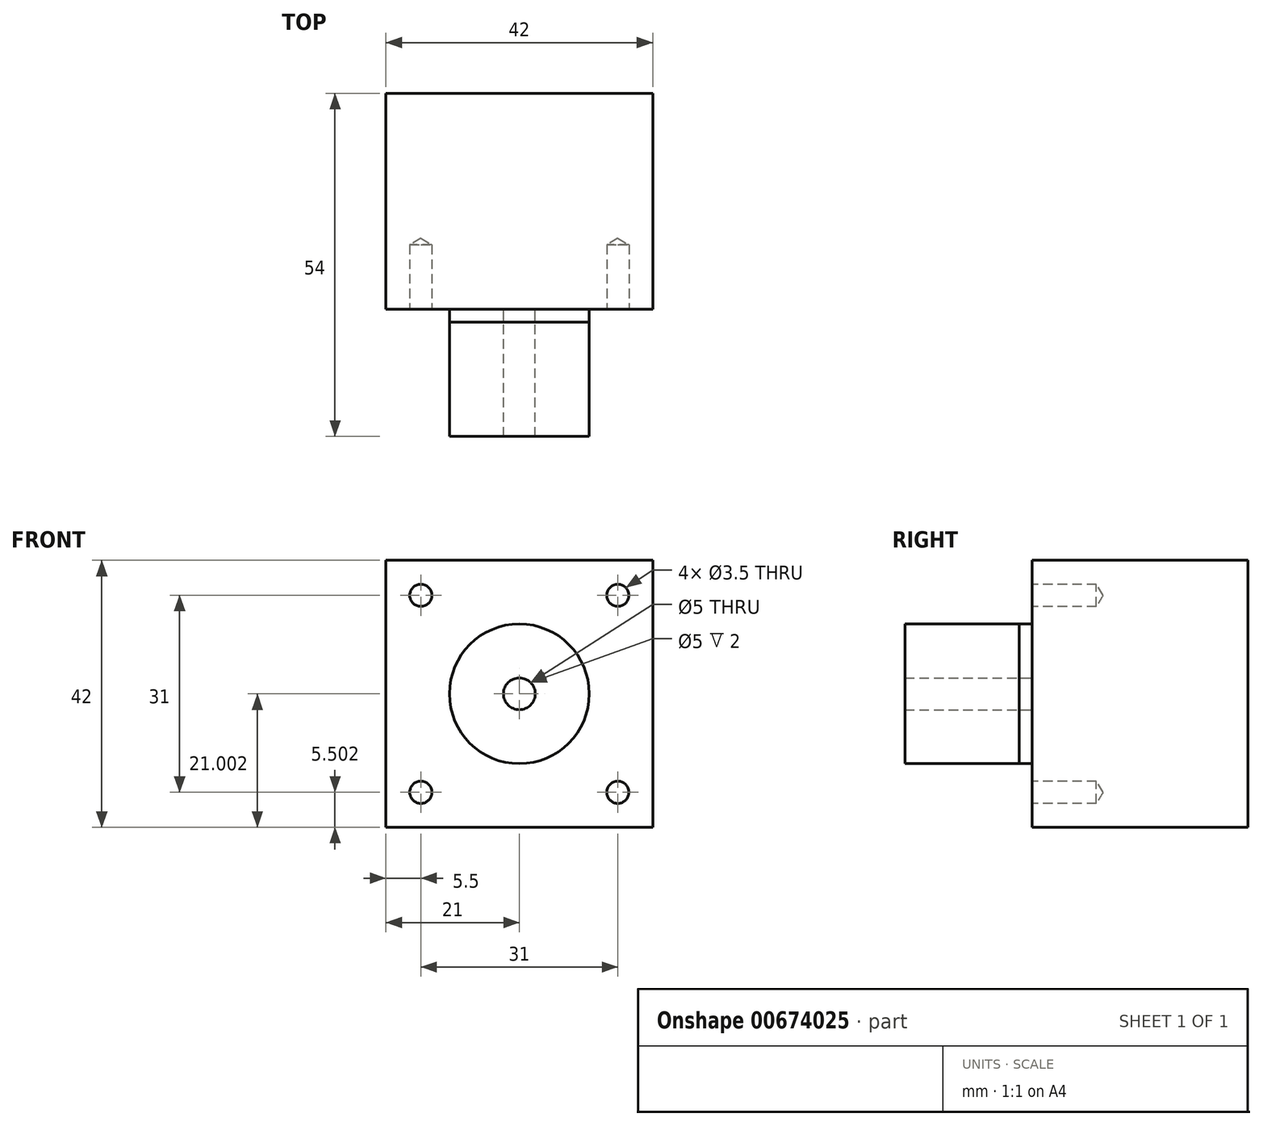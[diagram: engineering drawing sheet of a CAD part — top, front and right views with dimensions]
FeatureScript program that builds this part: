
annotation { "Feature Type Name" : "Feature", "Feature Type Description" : "" }
export const myFeature = defineFeature(function(context is Context, id is Id, definition is map)
    precondition{}
    {
        {
            var Q0;
            Q0=qCreatedBy(makeId("Right.planeOp"),FACE);
            var sketch = newSketch(context, id + "F0", { "sketchPlane" : qUnion([Q0])});
            skLineSegment(sketch, "E0.bottom", {"start": v(-63.29, 37.38) * mm, "end": v(-29.29, 37.38) * mm});
            skLineSegment(sketch, "E0.top", {"start": v(-63.29, 16.38) * mm, "end": v(-29.29, 16.38) * mm, "construction": true});
            skLineSegment(sketch, "E0.left", {"start": v(-63.29, 37.38) * mm, "end": v(-63.29, 16.38) * mm});
            skLineSegment(sketch, "E0.right", {"start": v(-29.29, 37.38) * mm, "end": v(-29.29, 16.38) * mm});
            skLineSegment(sketch, "E1.bottom", {"start": v(-63.29, 16.38) * mm, "end": v(-65.29, 16.38) * mm, "construction": true});
            skLineSegment(sketch, "E1.top", {"start": v(-63.29, 27.38) * mm, "end": v(-65.29, 27.38) * mm});
            skLineSegment(sketch, "E1.left", {"start": v(-63.29, 16.38) * mm, "end": v(-63.29, 27.38) * mm});
            skLineSegment(sketch, "E1.right", {"start": v(-65.29, 16.38) * mm, "end": v(-65.29, 27.38) * mm});
            skLineSegment(sketch, "E2.bottom", {"start": v(-65.29, 16.38) * mm, "end": v(-83.29, 16.38) * mm, "construction": true});
            skLineSegment(sketch, "E2.top", {"start": v(-65.29, 18.88) * mm, "end": v(-68.29, 18.88) * mm});
            skLineSegment(sketch, "E2.left", {"start": v(-65.29, 16.38) * mm, "end": v(-65.29, 18.88) * mm});
            skLineSegment(sketch, "E2.right", {"start": v(-83.29, 16.38) * mm, "end": v(-83.29, 18.38) * mm});
            skLineSegment(sketch, "E3.MirrorCS", {"start": v(-63.29, 5.38) * mm, "end": v(-65.29, 5.38) * mm});
            skLineSegment(sketch, "E4.MirrorCS", {"start": v(-63.29, 16.38) * mm, "end": v(-63.29, 5.38) * mm});
            skLineSegment(sketch, "E5.MirrorCS", {"start": v(-65.29, 16.38) * mm, "end": v(-65.29, 5.38) * mm});
            skLineSegment(sketch, "E6.MirrorCS", {"start": v(-29.29, -4.62) * mm, "end": v(-29.29, 16.38) * mm});
            skLineSegment(sketch, "E7.MirrorCS", {"start": v(-63.29, -4.62) * mm, "end": v(-29.29, -4.62) * mm});
            skLineSegment(sketch, "E8.MirrorCS", {"start": v(-65.29, 16.38) * mm, "end": v(-65.29, 13.88) * mm});
            skLineSegment(sketch, "E9.MirrorCS", {"start": v(-83.29, 16.38) * mm, "end": v(-83.29, 13.88) * mm});
            skLineSegment(sketch, "E10.MirrorCS", {"start": v(-65.29, 13.88) * mm, "end": v(-83.29, 13.88) * mm});
            skLineSegment(sketch, "E11.MirrorCS", {"start": v(-63.29, -4.62) * mm, "end": v(-63.29, 16.38) * mm});
            skLineSegment(sketch, "E12", {"start": v(-83.29, 18.38) * mm, "end": v(-68.29, 18.38) * mm});
            skLineSegment(sketch, "E13", {"start": v(-68.29, 18.38) * mm, "end": v(-68.29, 18.88) * mm});
            skSolve(sketch);
        }
        {
            var Q0;
            Q0=makeQuery(id+"F0.imprint","IMPRINT",FACE,{"disambiguationData":[TD([[makeQuery(id+"F0.imprint","IMPRINT",EDGE,{"derivedFrom":sQuery(id+"F0.wireOp",EDGE,"E0.bottom")}),-1.0]])]});
            extrude(context, id + "F1", {"entities" : qUnion([Q0]), "endBound" : BoundingType.SYMMETRIC, "depth" : 42 * mm, "offsetDistance" : 25.4 * mm});
        }
        {
            var Q0;
            Q0=makeQuery(id+"F1.opExtrude","SWEPT_FACE",FACE,{"disambiguationData":[OSD([sQuery(id+"F0.wireOp",EDGE,"E0.left"),sQuery(id+"F0.wireOp",EDGE,"E1.left"),sQuery(id+"F0.wireOp",EDGE,"E11.MirrorCS")])]});
            var sketch = newSketch(context, id + "F2", { "sketchPlane" : qUnion([Q0])});
            skLineSegment(sketch, "E14.0", {"start": v(0, 16.38) * mm, "end": v(0, 13.88) * mm});
            skLineSegment(sketch, "E15.0", {"start": v(0, 16.38) * mm, "end": v(0, 18.38) * mm});
            skLineSegment(sketch, "E16.0", {"start": v(0, 18.38) * mm, "end": v(0, 18.88) * mm});
            skLineSegment(sketch, "E17.0", {"start": v(0, 16.38) * mm, "end": v(0, 5.38) * mm});
            skLineSegment(sketch, "E18.0", {"start": v(0, 16.38) * mm, "end": v(0, 27.38) * mm});
            skCircle(sketch, "E19", {"center": v(0, 16.38) * mm, "radius": 11 * mm});
            skCircle(sketch, "E20", {"center": v(0, 16.38) * mm, "radius": 2.5 * mm});
            skSolve(sketch);
        }
        {
            var Q0;
            {var subQ0=sQuery(id+"F2.wireOp",EDGE,"E19");var subQ1=sQuery(id+"F2.wireOp",EDGE,"E17.0");var subQ2=makeQuery(id+"F2.imprint","INTERSECT",VERTEX,{"derivedFrom":[subQ1,subQ0]});Q0=makeQuery(id+"F2.imprint","IMPRINT",FACE,{"disambiguationData":[TD([[makeQuery(id+"F2.imprint","IMPRINT",EDGE,{"disambiguationData":[TD([[subQ2,1.0]])],"derivedFrom":subQ1}),-1.0]])]});}
            var Q1;
            {var subQ0=sQuery(id+"F2.wireOp",EDGE,"E19");var subQ1=sQuery(id+"F2.wireOp",EDGE,"E17.0");var subQ2=makeQuery(id+"F2.imprint","INTERSECT",VERTEX,{"derivedFrom":[subQ1,subQ0]});Q1=makeQuery(id+"F2.imprint","IMPRINT",FACE,{"disambiguationData":[TD([[makeQuery(id+"F2.imprint","IMPRINT",EDGE,{"disambiguationData":[TD([[subQ2,1.0]])],"derivedFrom":subQ1}),1.0]])]});}
            extrude(context, id + "F3", {"entities" : qUnion([Q0, Q1]), "operationType" : NewBodyOperationType.ADD, "depth" : 2 * mm, "offsetDistance" : 25.4 * mm});
        }
        {
            var Q0;
            {var subQ0=sQuery(id+"F2.wireOp",EDGE,"E18.0");var subQ1=sQuery(id+"F2.wireOp",EDGE,"E17.0");var subQ2=makeQuery(id+"F2.imprint","INTERSECT",VERTEX,{"derivedFrom":[subQ1,subQ0]});Q0=makeQuery(id+"F2.imprint","IMPRINT",FACE,{"disambiguationData":[TD([[makeQuery(id+"F2.imprint","IMPRINT",EDGE,{"disambiguationData":[TD([[subQ2,-1.0]])],"derivedFrom":subQ1}),-1.0]])]});}
            var Q1;
            {var subQ0=sQuery(id+"F2.wireOp",EDGE,"E18.0");var subQ1=sQuery(id+"F2.wireOp",EDGE,"E17.0");var subQ2=makeQuery(id+"F2.imprint","INTERSECT",VERTEX,{"derivedFrom":[subQ1,subQ0]});Q1=makeQuery(id+"F2.imprint","IMPRINT",FACE,{"disambiguationData":[TD([[makeQuery(id+"F2.imprint","IMPRINT",EDGE,{"disambiguationData":[TD([[subQ2,-1.0]])],"derivedFrom":subQ1}),1.0]])]});}
            extrude(context, id + "F4", {"entities" : qUnion([Q0, Q1]), "depth" : 20 * mm, "offsetDistance" : 25.4 * mm});
        }
        {
            var Q0;
            Q0=makeQuery(id+"F4.opExtrude","CAP_FACE",FACE,{"disambiguationData":[OSD([sQuery(id+"F2.wireOp",EDGE,"E20")])],"isStart":false});
            var sketch = newSketch(context, id + "F5", { "sketchPlane" : qUnion([Q0])});
            skLineSegment(sketch, "E21", {"start": v(-1.5, 18.38) * mm, "end": v(1.5, 18.38) * mm});
            skSolve(sketch);
        }
        {
            var Q0;
            {var subQ0=sQuery(id+"F5.wireOp",EDGE,"E21");Q0=makeQuery(id+"F5.imprint","IMPRINT",FACE,{"disambiguationData":[TD([[makeQuery(id+"F5.imprint","IMPRINT",EDGE,{"derivedFrom":subQ0}),1.0]])]});}
            extrude(context, id + "F6", {"entities" : qUnion([Q0]), "operationType" : NewBodyOperationType.REMOVE, "oppositeDirection" : true, "depth" : 15 * mm, "offsetDistance" : 25.4 * mm});
        }
        {
            var Q0;
            {var subQ0=sQuery(id+"F0.wireOp",EDGE,"E0.left");Q0=makeQuery(id+"F2.imprint","IMPRINT",FACE,{"disambiguationData":[TD([[makeQuery(id+"F2.imprint","IMPRINT",EDGE,{"derivedFrom":makeQuery(id+"F1.opExtrude","SWEPT_EDGE",EDGE,{"disambiguationData":[OSD([sQuery(id+"F0.wireOp",EDGE,"E0.bottom"),subQ0])]})}),1.0]])]});}
            var sketch = newSketch(context, id + "F7", { "sketchPlane" : qUnion([Q0])});
            skCircle(sketch, "E22", {"center": v(-15.5, 31.88) * mm, "radius": 1.75 * mm});
            skCircle(sketch, "E23", {"center": v(-15.5, 0.88) * mm, "radius": 1.75 * mm});
            skCircle(sketch, "E24", {"center": v(15.5, 0.88) * mm, "radius": 1.75 * mm});
            skCircle(sketch, "E25", {"center": v(15.5, 31.88) * mm, "radius": 1.75 * mm});
            skLineSegment(sketch, "E26", {"start": v(-15.5, 31.88) * mm, "end": v(15.5, 31.88) * mm, "construction": true});
            skLineSegment(sketch, "E27", {"start": v(15.5, 31.88) * mm, "end": v(15.5, 0.88) * mm, "construction": true});
            skLineSegment(sketch, "E28", {"start": v(-15.5, 0.88) * mm, "end": v(15.5, 0.88) * mm, "construction": true});
            skLineSegment(sketch, "E29", {"start": v(-15.5, 31.88) * mm, "end": v(-15.5, 0.88) * mm, "construction": true});
            skCircle(sketch, "E30.0", {"center": v(0, 16.38) * mm, "radius": 11 * mm, "construction": true});
            skPoint(sketch, "E31", {"position": v(-15.5, 16.38) * mm});
            skPoint(sketch, "E32", {"position": v(0, 0.88) * mm});
            skPoint(sketch, "E33", {"position": v(15.5, 16.38) * mm});
            skPoint(sketch, "E34", {"position": v(0, 31.88) * mm});
            skLineSegment(sketch, "E35", {"start": v(0, 31.88) * mm, "end": v(0, 16.38) * mm, "construction": true});
            skLineSegment(sketch, "E36", {"start": v(-15.5, 16.38) * mm, "end": v(0, 16.38) * mm, "construction": true});
            skSolve(sketch);
        }
        {
            var Q0;
            Q0=sQuery(id+"F7.wireOp",VERTEX,"E26.start");
            var Q1;
            Q1=sQuery(id+"F7.wireOp",VERTEX,"E26.end");
            var Q2;
            Q2=sQuery(id+"F7.wireOp",VERTEX,"E27.end");
            var Q3;
            Q3=sQuery(id+"F7.wireOp",VERTEX,"E28.start");
            var Q4;
            Q4=makeQuery(id+"F1.opExtrude","SWEPT_BODY",BODY,{"disambiguationData":[OSD([sQuery(id+"F0.wireOp",EDGE,"E0.bottom"),sQuery(id+"F0.wireOp",EDGE,"E0.left"),sQuery(id+"F0.wireOp",EDGE,"E0.right"),sQuery(id+"F0.wireOp",EDGE,"E1.left"),sQuery(id+"F0.wireOp",EDGE,"E6.MirrorCS"),sQuery(id+"F0.wireOp",EDGE,"E7.MirrorCS"),sQuery(id+"F0.wireOp",EDGE,"E11.MirrorCS")])]});
            hole(context, id + "F8", {"style" : HoleStyle.SIMPLE, "endStyle" : HoleEndStyle.BLIND, "holeDiameter" : 3.5 * mm, "majorDiameter" : 3 * mm, "holeDepth" : 10.16 * mm, "isTappedThrough" : true, "tappedDepth" : 12.7 * mm, "tapClearance" : 3, "locations" : qUnion([Q0, Q1, Q2, Q3]), "scope" : qUnion([Q4])});
        }
    });
